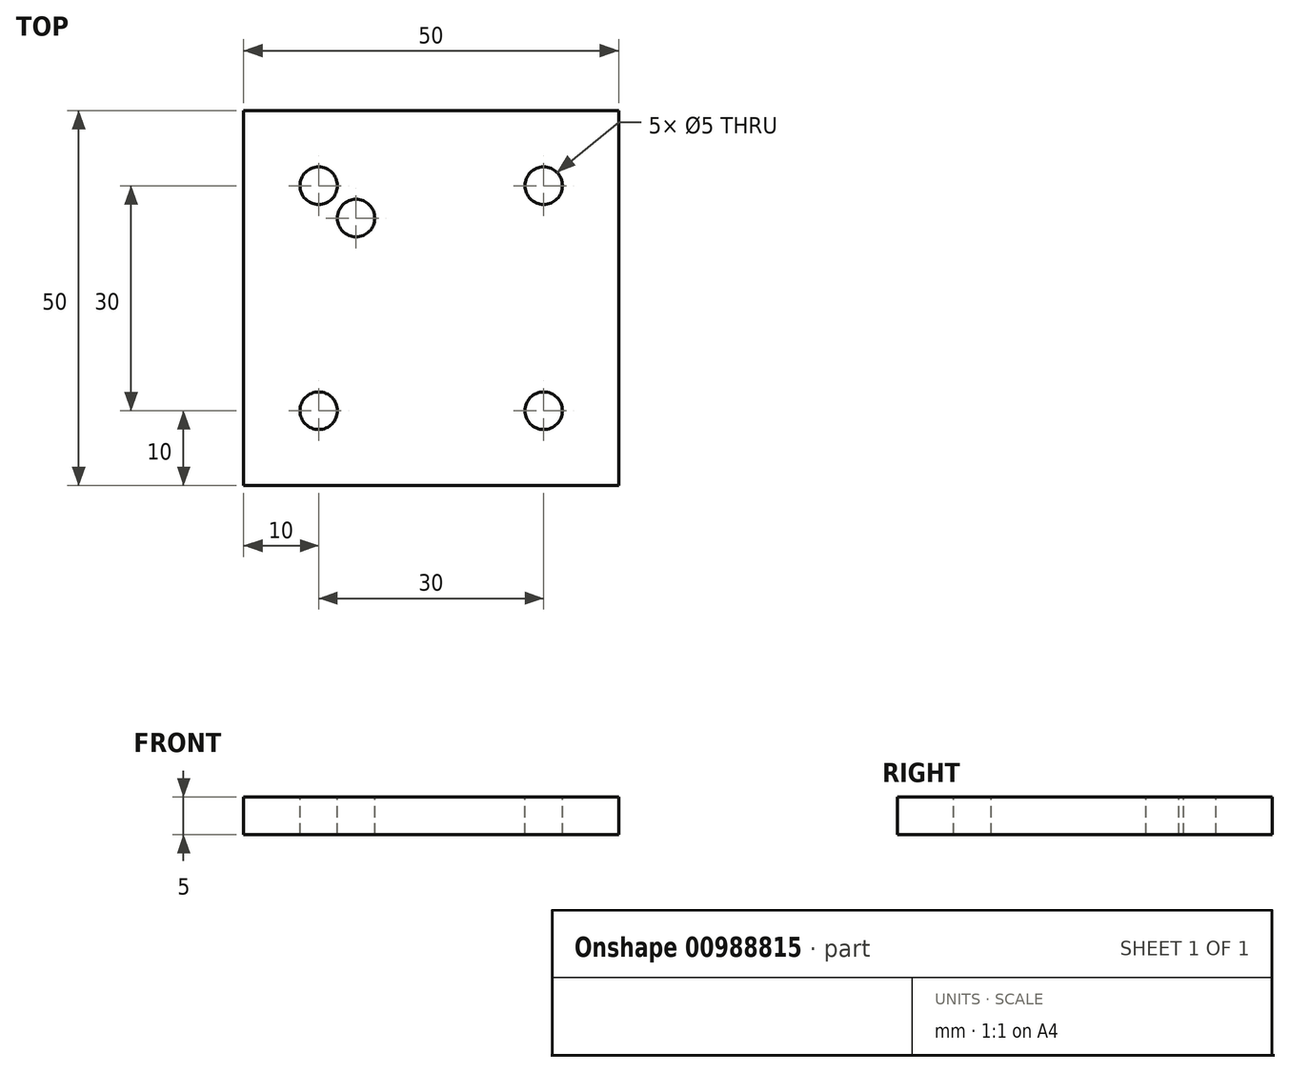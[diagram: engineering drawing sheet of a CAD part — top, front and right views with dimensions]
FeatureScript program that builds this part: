
annotation { "Feature Type Name" : "Feature", "Feature Type Description" : "" }
export const myFeature = defineFeature(function(context is Context, id is Id, definition is map)
    precondition{}
    {
        {
            var Q0;
            Q0=qCreatedBy(makeId("Top.planeOp"),FACE);
            var sketch = newSketch(context, id + "F0", { "sketchPlane" : qUnion([Q0])});
            skLineSegment(sketch, "E0.bottom", {"start": v(-25, 25) * mm, "end": v(25, 25) * mm});
            skLineSegment(sketch, "E0.top", {"start": v(-25, -25) * mm, "end": v(25, -25) * mm});
            skLineSegment(sketch, "E0.left", {"start": v(-25, 25) * mm, "end": v(-25, -25) * mm});
            skLineSegment(sketch, "E0.right", {"start": v(25, 25) * mm, "end": v(25, -25) * mm});
            skPoint(sketch, "E0.middle", {"position": v(0, 0) * mm});
            skSolve(sketch);
        }
        {
            var Q0;
            Q0=qSketchRegion(id+"F0",true);
            extrude(context, id + "F1", {"entities" : qUnion([Q0]), "depth" : 5 * mm, "offsetDistance" : 25 * mm});
        }
        {
            var Q0;
            Q0=makeQuery(id+"F1.opExtrude","CAP_FACE",FACE,{"disambiguationData":[OSD([sQuery(id+"F0.wireOp",EDGE,"E0.bottom"),sQuery(id+"F0.wireOp",EDGE,"E0.top"),sQuery(id+"F0.wireOp",EDGE,"E0.left"),sQuery(id+"F0.wireOp",EDGE,"E0.right")])],"isStart":false});
            var sketch = newSketch(context, id + "F2", { "sketchPlane" : qUnion([Q0])});
            skPoint(sketch, "E1", {"position": v(-10.02, 10.67) * mm});
            skSolve(sketch);
        }
        {
            var Q0;
            Q0=sQuery(id+"F2.wireOp",VERTEX,"E1");
            var Q1;
            Q1=makeQuery(id+"F1.opExtrude","SWEPT_BODY",BODY,{"disambiguationData":[OSD([sQuery(id+"F0.wireOp",EDGE,"E0.bottom"),sQuery(id+"F0.wireOp",EDGE,"E0.top"),sQuery(id+"F0.wireOp",EDGE,"E0.left"),sQuery(id+"F0.wireOp",EDGE,"E0.right")])]});
            hole(context, id + "F3", {"style" : HoleStyle.SIMPLE, "endStyle" : HoleEndStyle.THROUGH, "holeDiameter" : 5 * mm, "majorDiameter" : 5 * mm, "isTappedThrough" : true, "tappedDepth" : 12 * mm, "tapClearance" : 3, "locations" : qUnion([Q0]), "scope" : qUnion([Q1])});
        }
        {
            var Q0;
            Q0=makeQuery(id+"F1.opExtrude","CAP_FACE",FACE,{"disambiguationData":[OSD([sQuery(id+"F0.wireOp",EDGE,"E0.bottom"),sQuery(id+"F0.wireOp",EDGE,"E0.top"),sQuery(id+"F0.wireOp",EDGE,"E0.left"),sQuery(id+"F0.wireOp",EDGE,"E0.right")])],"isStart":false});
            var sketch = newSketch(context, id + "F4", { "sketchPlane" : qUnion([Q0])});
            skPoint(sketch, "E2", {"position": v(-15, 15) * mm});
            skLineSegment(sketch, "E3", {"start": v(0, 0) * mm, "end": v(-25, 0) * mm, "construction": true});
            skLineSegment(sketch, "E4", {"start": v(-25, 0) * mm, "end": v(25, 0) * mm, "construction": true});
            skLineSegment(sketch, "E5", {"start": v(0, 25) * mm, "end": v(0, -25) * mm, "construction": true});
            skPoint(sketch, "E6.MirrorP", {"position": v(15, 15) * mm});
            skPoint(sketch, "E7.MirrorP", {"position": v(15, -15) * mm});
            skPoint(sketch, "E8.MirrorP", {"position": v(-15, -15) * mm});
            skSolve(sketch);
        }
        {
            var Q0;
            Q0=sQuery(id+"F4.wireOp",VERTEX,"E2");
            var Q1;
            Q1=sQuery(id+"F4.wireOp",VERTEX,"E6.MirrorP");
            var Q2;
            Q2=sQuery(id+"F4.wireOp",VERTEX,"E7.MirrorP");
            var Q3;
            Q3=sQuery(id+"F4.wireOp",VERTEX,"E8.MirrorP");
            var Q4;
            Q4=makeQuery(id+"F1.opExtrude","SWEPT_BODY",BODY,{"disambiguationData":[OSD([sQuery(id+"F0.wireOp",EDGE,"E0.bottom"),sQuery(id+"F0.wireOp",EDGE,"E0.top"),sQuery(id+"F0.wireOp",EDGE,"E0.left"),sQuery(id+"F0.wireOp",EDGE,"E0.right")])]});
            hole(context, id + "F5", {"style" : HoleStyle.SIMPLE, "endStyle" : HoleEndStyle.THROUGH, "holeDiameter" : 5 * mm, "majorDiameter" : 5 * mm, "isTappedThrough" : true, "tappedDepth" : 12 * mm, "tapClearance" : 3, "locations" : qUnion([Q0, Q1, Q2, Q3]), "scope" : qUnion([Q4])});
        }
    });
